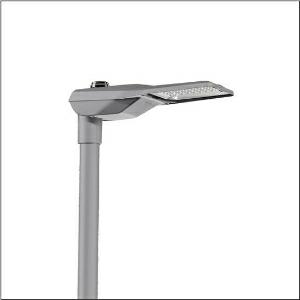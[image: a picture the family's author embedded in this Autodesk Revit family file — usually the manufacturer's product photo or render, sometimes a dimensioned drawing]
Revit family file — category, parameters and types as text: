
# Revit family: streetlight_sl_21_mini___st0_8a_5xe6c47n08gb_7d6b
name_source: partatom
category: Lighting Fixtures
units: mm (PartAtom-declared; Revit-internal decimal feet)

## family parameters
Cut with Voids When Loaded = No
Host = Face
Light Source = No
Part Type = Normal
Room Calculation Point = No
Round Connector Dimension = Use Diameter
Shared = No

## types (1)
- --- (1 x LED, 6180 lm, 40.4 W, 4000K)
    Apparent Load = 40 VA
    CIE Flux Codes = 38 75 97 100 100
    Color Rendering = 70
    Color Temperature = 4000K
    Default Elevation = 1800 mm
    Description = Streetlight SL 21 mini, mast luminaire, primary light control with lens, of PMMA, primary optical cover: cover, of toughened safety glass, transparent, light distribution: ST0.8a, light emission: direct distribution, primary light characteristic: asymmetric, installation type: side-entry, LED, 3G 1.5mm², High Power LED, rated luminous flux: 6.180lm, luminous efficacy: 153lm/W, light colour: 740, colour temperature: 4000K, control gear: NEMA (7pin), control: overheat protection, pre-setting: linear dimming characteristic, constant luminous flux control, time-dependent luminous flux control, flexible luminous flux parameterisation, mains connection: 230..240V, AC, 50/60Hz, connection cable pre-assembled, cable length: 8,5m, wiring characteristics: H07RN-F, start of lifetime: 40W, end of service life: 41W, reduction: 19W, luminaire housing, of diecast aluminium (EN AC-44300), powder-coated, SITECO metallic grey (DB 702S), corrosivity category C5 high according to DIN EN ISO 12944, multi-level sealing system, sealing non-destructively replaceable, inclination adjustable: 0°, 5°, 10°, 15°, length: 628mm, width: 235mm, height: 110mm, spigot size: 42mm (side-entry), mounting height: 4..8m, protection rating (complete): IP66, insulation class (complete): insulation class I (protective earthing), certification: CE, ENEC, ENEC+, VDE, impact resistance: IK10, permissible operating ambient temperature for outdoor applications: -40..+50°C, standard-compliant lighting for roads and squares, packaging unit: 1 piece

Light Distribution: ST0.8a
    Height = 110 mm
    Lamp = 1 x LED
    Lamp Light Flux = 6180 lm
    Lamp Power = 40.4 W
    Lamp count = 1
    Length = 625 mm
    Luminous efficacy = 153 lm/W
    Manufacturer = Siteco
    ModVariant = No
    Model = 5XE6C47N08GB
    Number of Poles = 1
    OnlyDefault = Yes
    Power Factor = 1
    Product Name = Streetlight SL 21 mini | ST0.8a
    Product group = mast luminaire | pylon top
    ProductGroupID = 6100
    Protection Class = Protection class I
    Protection Degree = IP 66
    RLX_Detail_Level = 1
    RLX_Emergency_Light_Flux = 0 lm
    RLX_Emergency_Type = 0
    RLX_Emergency_Type_DB = No
    RlxData = <blob elided: 25865 chars, md5=a0ccabfe>
    Socket = socket
    Standby Power = 0 W
    System Light Flux = 6180 lm
    System Power = 40 W
    Type Comments = factory setting: luminous flux: 100 % | dim-lin: 254 | 812 mA
    Type Image = l_1294379.jpg
    URL = http://relux.com
    VarID = @adj_133683
    Voltage = 0 V
    Weight = 0.00 kg
    Width = 234 mm

## geometry (parser evidence)
native form markers: Blend x4, Sweep x13
no freeform markers — native parametric forms only
